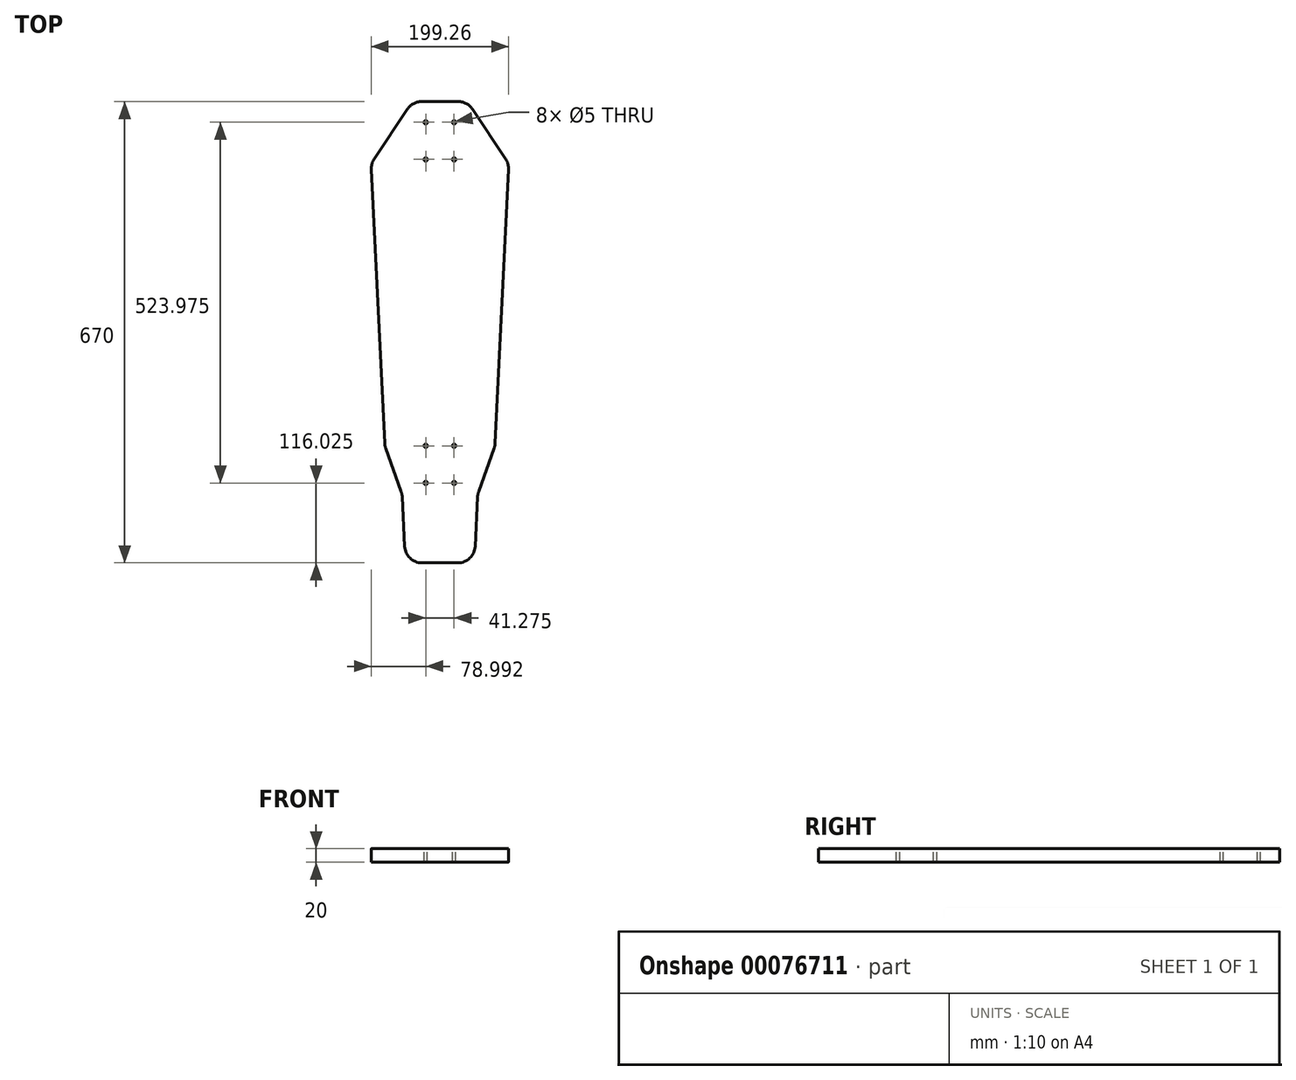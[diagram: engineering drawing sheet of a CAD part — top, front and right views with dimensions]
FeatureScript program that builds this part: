
annotation { "Feature Type Name" : "Feature", "Feature Type Description" : "" }
export const myFeature = defineFeature(function(context is Context, id is Id, definition is map)
    precondition{}
    {
        {
            var Q0;
            Q0=qCreatedBy(makeId("Top.planeOp"),FACE);
            var sketch = newSketch(context, id + "F0", { "sketchPlane" : qUnion([Q0])});
            skLineSegment(sketch, "E0.bottom", {"start": v(-100, 335) * mm, "end": v(100, 335) * mm});
            skLineSegment(sketch, "E0.top", {"start": v(-100, -335) * mm, "end": v(100, -335) * mm});
            skLineSegment(sketch, "E0.left", {"start": v(-100, 335) * mm, "end": v(-100, -335) * mm});
            skLineSegment(sketch, "E0.right", {"start": v(100, 335) * mm, "end": v(100, -335) * mm});
            skPoint(sketch, "E0.middle", {"position": v(0, 0) * mm});
            skLineSegment(sketch, "E1.bottom", {"start": v(-20.64, 305) * mm, "end": v(20.64, 305) * mm, "construction": true});
            skLineSegment(sketch, "E1.top", {"start": v(-20.64, 251.02) * mm, "end": v(20.64, 251.02) * mm, "construction": true});
            skLineSegment(sketch, "E1.left", {"start": v(-20.64, 305) * mm, "end": v(-20.64, 251.02) * mm, "construction": true});
            skLineSegment(sketch, "E1.right", {"start": v(20.64, 305) * mm, "end": v(20.64, 251.02) * mm, "construction": true});
            skLineSegment(sketch, "E2", {"start": v(0, 335) * mm, "end": v(0, -335) * mm});
            skPoint(sketch, "E3", {"position": v(0, 305) * mm});
            skPoint(sketch, "E4", {"position": v(0, 251.02) * mm});
            skLineSegment(sketch, "E5", {"start": v(-20.64, 305) * mm, "end": v(20.64, 251.02) * mm, "construction": true});
            skPoint(sketch, "E6", {"position": v(0, 278.01) * mm});
            skCircle(sketch, "E7", {"center": v(-20.64, 305) * mm, "radius": 2.5 * mm});
            skCircle(sketch, "E8", {"center": v(20.64, 305) * mm, "radius": 2.5 * mm});
            skCircle(sketch, "E9", {"center": v(20.64, 251.02) * mm, "radius": 2.5 * mm});
            skCircle(sketch, "E10", {"center": v(-20.64, 251.02) * mm, "radius": 2.5 * mm});
            skLineSegment(sketch, "E11.bottom", {"start": v(-20.64, -165) * mm, "end": v(20.64, -165) * mm, "construction": true});
            skLineSegment(sketch, "E11.top", {"start": v(-20.64, -218.98) * mm, "end": v(20.64, -218.98) * mm, "construction": true});
            skLineSegment(sketch, "E11.left", {"start": v(-20.64, -165) * mm, "end": v(-20.64, -218.98) * mm, "construction": true});
            skLineSegment(sketch, "E11.right", {"start": v(20.64, -165) * mm, "end": v(20.64, -218.98) * mm, "construction": true});
            skPoint(sketch, "E12", {"position": v(0, -165) * mm});
            skPoint(sketch, "E13", {"position": v(0, -218.98) * mm});
            skLineSegment(sketch, "E14", {"start": v(-20.64, -165) * mm, "end": v(20.64, -218.98) * mm, "construction": true});
            skPoint(sketch, "E15", {"position": v(0, -191.99) * mm});
            skCircle(sketch, "E16", {"center": v(-20.64, -165) * mm, "radius": 2.5 * mm});
            skCircle(sketch, "E17", {"center": v(20.64, -165) * mm, "radius": 2.5 * mm});
            skCircle(sketch, "E18", {"center": v(20.64, -218.98) * mm, "radius": 2.5 * mm});
            skCircle(sketch, "E19", {"center": v(-20.64, -218.98) * mm, "radius": 2.5 * mm});
            skSolve(sketch);
        }
        {
            var Q0;
            Q0=qCreatedBy(makeId("Right.planeOp"),FACE);
            var sketch = newSketch(context, id + "F1", { "sketchPlane" : qUnion([Q0])});
            skLineSegment(sketch, "E20", {"start": v(-205.67, 0) * mm, "end": v(335, 0) * mm});
            skLineSegment(sketch, "E21", {"start": v(-257.43, 6.81) * mm, "end": v(-335, 27.6) * mm});
            skLineSegment(sketch, "E22", {"start": v(-232, 0) * mm, "end": v(-346.12, 0) * mm, "construction": true});
            skPoint(sketch, "E23.visualSharp", {"position": v(-232, 0) * mm});
            skArc(sketch, "E23.filletArc", {"start": v(-257.43, 6.81) * mm, "mid": v(-231.77, 1.71) * mm, "end": v(-205.67, 0) * mm});
            skSolve(sketch);
        }
        {
            var Q0;
            Q0 = qSketchRegion(id + "F0", true);
            extrude(context, id + "F2", {"entities" : qUnion([Q0]), "oppositeDirection" : true, "depth" : 20 * mm});
        }
        {
            var Q0;
            Q0=makeQuery(id+"F2.opExtrude","CAP_FACE",FACE,{"disambiguationData":[OSD([sQuery(id+"F0.wireOp",EDGE,"E0.bottom"),sQuery(id+"F0.wireOp",EDGE,"E0.top"),sQuery(id+"F0.wireOp",EDGE,"E0.left"),sQuery(id+"F0.wireOp",EDGE,"E0.right"),sQuery(id+"F0.wireOp",EDGE,"E7"),sQuery(id+"F0.wireOp",EDGE,"E8"),sQuery(id+"F0.wireOp",EDGE,"E9"),sQuery(id+"F0.wireOp",EDGE,"E10"),sQuery(id+"F0.wireOp",EDGE,"E16"),sQuery(id+"F0.wireOp",EDGE,"E17"),sQuery(id+"F0.wireOp",EDGE,"E18"),sQuery(id+"F0.wireOp",EDGE,"E19")])],"isStart":true});
            var sketch = newSketch(context, id + "F3", { "sketchPlane" : qUnion([Q0])});
            skLineSegment(sketch, "E24", {"start": v(-47.42, 323.87) * mm, "end": v(-95.43, 251.86) * mm});
            skLineSegment(sketch, "E25", {"start": v(-99.6, 236.77) * mm, "end": v(-80.18, -161.3) * mm});
            skLineSegment(sketch, "E26", {"start": v(-78.75, -168.49) * mm, "end": v(-56.24, -231.53) * mm});
            skLineSegment(sketch, "E27", {"start": v(-54.82, -238.69) * mm, "end": v(-51.19, -311.25) * mm});
            skPoint(sketch, "E28.visualSharp", {"position": v(-55, -235) * mm});
            skArc(sketch, "E28.filletArc", {"start": v(-54.82, -238.69) * mm, "mid": v(-55.27, -235.05) * mm, "end": v(-56.24, -231.53) * mm});
            skPoint(sketch, "E29.visualSharp", {"position": v(-80, -165) * mm});
            skArc(sketch, "E29.filletArc", {"start": v(-80.18, -161.3) * mm, "mid": v(-79.73, -164.95) * mm, "end": v(-78.75, -168.49) * mm});
            skPoint(sketch, "E30.visualSharp", {"position": v(-100, 245) * mm});
            skArc(sketch, "E30.filletArc", {"start": v(-95.43, 251.86) * mm, "mid": v(-98.72, 244.65) * mm, "end": v(-99.6, 236.77) * mm});
            skLineSegment(sketch, "E31.MirrorCS", {"start": v(47.42, 323.87) * mm, "end": v(95.43, 251.86) * mm});
            skArc(sketch, "E32.MirrorCS", {"start": v(95.43, 251.86) * mm, "mid": v(98.72, 244.65) * mm, "end": v(99.6, 236.77) * mm});
            skLineSegment(sketch, "E33.MirrorCS", {"start": v(99.6, 236.77) * mm, "end": v(80.18, -161.3) * mm});
            skArc(sketch, "E34.MirrorCS", {"start": v(80.18, -161.3) * mm, "mid": v(79.73, -164.95) * mm, "end": v(78.75, -168.49) * mm});
            skLineSegment(sketch, "E35.MirrorCS", {"start": v(78.75, -168.49) * mm, "end": v(56.24, -231.53) * mm});
            skArc(sketch, "E36.MirrorCS", {"start": v(54.82, -238.69) * mm, "mid": v(55.27, -235.05) * mm, "end": v(56.24, -231.53) * mm});
            skLineSegment(sketch, "E37.MirrorCS", {"start": v(54.82, -238.69) * mm, "end": v(51.19, -311.25) * mm});
            skLineSegment(sketch, "E38", {"start": v(-26.22, -335) * mm, "end": v(26.22, -335) * mm});
            skLineSegment(sketch, "E39", {"start": v(-26.62, 335) * mm, "end": v(26.62, 335) * mm});
            skPoint(sketch, "E40.visualSharp", {"position": v(-40, 335) * mm});
            skArc(sketch, "E40.filletArc", {"start": v(-26.62, 335) * mm, "mid": v(-38.42, 332.04) * mm, "end": v(-47.42, 323.87) * mm});
            skPoint(sketch, "E41.visualSharp", {"position": v(40, 335) * mm});
            skArc(sketch, "E41.filletArc", {"start": v(47.42, 323.87) * mm, "mid": v(38.42, 332.04) * mm, "end": v(26.62, 335) * mm});
            skPoint(sketch, "E42.visualSharp", {"position": v(50, -335) * mm});
            skArc(sketch, "E42.filletArc", {"start": v(26.22, -335) * mm, "mid": v(43.45, -328.11) * mm, "end": v(51.19, -311.25) * mm});
            skPoint(sketch, "E43.visualSharp", {"position": v(-50, -335) * mm});
            skArc(sketch, "E43.filletArc", {"start": v(-51.19, -311.25) * mm, "mid": v(-43.45, -328.11) * mm, "end": v(-26.22, -335) * mm});
            skSolve(sketch);
        }
        {
            var Q0;
            Q0 = qSketchRegion(id + "F3", true);
            extrude(context, id + "F4", {"entities" : qUnion([Q0]), "operationType" : NewBodyOperationType.INTERSECT, "endBound" : BoundingType.THROUGH_ALL, "oppositeDirection" : true, "depth" : 25 * mm});
        }
    });
